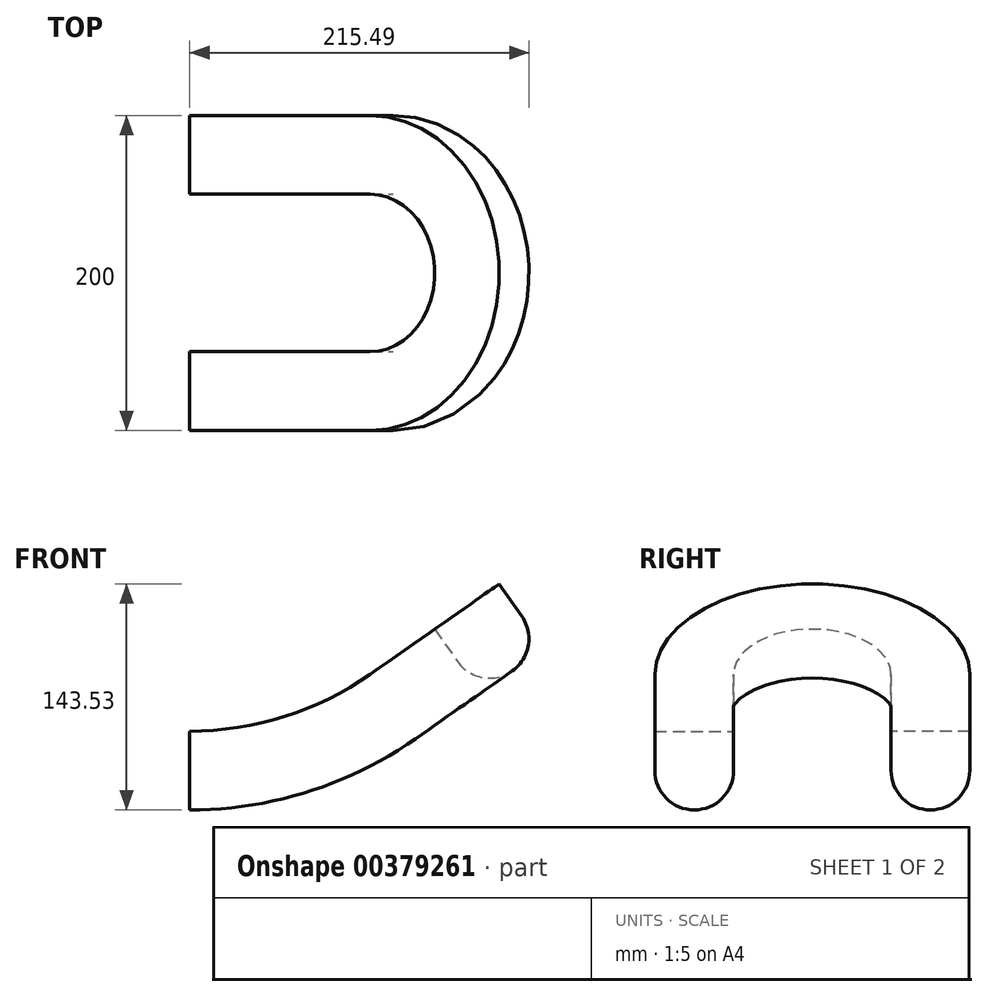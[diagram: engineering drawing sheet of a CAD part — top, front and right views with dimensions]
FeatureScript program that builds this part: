
annotation { "Feature Type Name" : "Feature", "Feature Type Description" : "" }
export const myFeature = defineFeature(function(context is Context, id is Id, definition is map)
    precondition{}
    {
        {
            var Q0;
            Q0=qCreatedBy(makeId("Front.planeOp"),FACE);
            var sketch = newSketch(context, id + "F0", { "sketchPlane" : qUnion([Q0])});
            skArc(sketch, "E0", {"start": v(114.72, -163.83) * mm, "mid": v(60.14, -190.74) * mm, "end": v(0, -200) * mm});
            skLineSegment(sketch, "E1", {"start": v(0, 0) * mm, "end": v(0, -200) * mm});
            skLineSegment(sketch, "E2", {"start": v(0, 0) * mm, "end": v(114.72, -163.83) * mm, "construction": true});
            skLineSegment(sketch, "E3", {"start": v(0, 0) * mm, "end": v(-114.72, -163.83) * mm, "construction": true});
            skArc(sketch, "E4", {"start": v(0, -200) * mm, "mid": v(-60.14, -190.74) * mm, "end": v(-114.72, -163.83) * mm, "construction": true});
            skLineSegment(sketch, "E5", {"start": v(114.72, -163.83) * mm, "end": v(196.63, -106.47) * mm});
            skLineSegment(sketch, "E6", {"start": v(-114.72, -163.83) * mm, "end": v(-196.63, -106.47) * mm, "construction": true});
            skSolve(sketch);
        }
        {
            var Q0;
            Q0=sQuery(id+"F0.wireOp",EDGE,"E5");
            var Q1;
            Q1=sQuery(id+"F0.wireOp",EDGE,"E0");
            extrude(context, id + "F1", {"bodyType" : ToolBodyType.SURFACE, "surfaceEntities" : qUnion([Q0, Q1]), "depth" : 100 * mm});
        }
        {
            var Q0;
            Q0=makeQuery(id+"F1.opExtrude","SWEPT_FACE",FACE,{"disambiguationData":[OSD([sQuery(id+"F0.wireOp",EDGE,"E5")])]});
            var sketch = newSketch(context, id + "F2", { "sketchPlane" : qUnion([Q0])});
            skArc(sketch, "E7", {"start": v(100, 100) * mm, "mid": v(70.71, 29.29) * mm, "end": v(0, 0) * mm});
            skSolve(sketch);
        }
        {
            var Q0;
            Q0=qCreatedBy(makeId("Right.planeOp"),FACE);
            var sketch = newSketch(context, id + "F3", { "sketchPlane" : qUnion([Q0])});
            skLineSegment(sketch, "E8.bottom", {"start": v(0, -200) * mm, "end": v(-50, -200) * mm});
            skLineSegment(sketch, "E8.top", {"start": v(0, -225) * mm, "end": v(-50, -225) * mm, "construction": true});
            skLineSegment(sketch, "E8.left", {"start": v(0, -200) * mm, "end": v(0, -225) * mm});
            skLineSegment(sketch, "E8.right", {"start": v(-50, -200) * mm, "end": v(-50, -225) * mm});
            skArc(sketch, "E9", {"start": v(0, -225) * mm, "mid": v(-25, -250) * mm, "end": v(-50, -225) * mm});
            skSolve(sketch);
        }
        {
            var Q0;
            Q0=makeQuery(id+"F3.imprint","IMPRINT",FACE,{"disambiguationData":[TD([[makeQuery(id+"F3.imprint","IMPRINT",EDGE,{"derivedFrom":sQuery(id+"F3.wireOp",EDGE,"E8.bottom")}),1.0]])]});
            var Q1;
            Q1=makeQuery(id+"F1.opExtrude","CAP_EDGE",EDGE,{"disambiguationData":[OSD([sQuery(id+"F0.wireOp",EDGE,"E0")])],"isStart":true});
            var Q2;
            Q2=sQuery(id+"F2.wireOp",EDGE,"E7");
            sweep(context, id + "F4", {"profiles" : qUnion([Q0]), "path" : qUnion([Q1, Q2])});
        }
        {
            var Q0;
            Q0=makeQuery(id+"F1.opExtrude","CAP_VERTEX",VERTEX,{"disambiguationData":[OSD([sQuery(id+"F0.wireOp",VERTEX,"E5.end")])],"isStart":false});
            var Q1;
            Q1=makeQuery(id+"F1.opExtrude","CAP_VERTEX",VERTEX,{"disambiguationData":[OSD([sQuery(id+"F0.wireOp",VERTEX,"E0.start")])],"isStart":false});
            var Q2;
            Q2=makeQuery(id+"F1.opExtrude","CAP_VERTEX",VERTEX,{"disambiguationData":[OSD([sQuery(id+"F0.wireOp",VERTEX,"E0.end")])],"isStart":false});
            cPlane(context, id + "F5", {"entities" : qUnion([Q0, Q1, Q2]), "cplaneType" : CPlaneType.THREE_POINT, "offset" : 25 * mm, "width" : 150 * mm, "height" : 150 * mm});
        }
        {
            var Q0;
            Q0=makeQuery(id+"F4.opSweep","SWEPT_BODY",BODY,{"disambiguationData":[OSD([sQuery(id+"F2.wireOp",EDGE,"E7"),sQuery(id+"F3.wireOp",EDGE,"E8.bottom"),sQuery(id+"F3.wireOp",EDGE,"E8.left"),sQuery(id+"F3.wireOp",EDGE,"E8.right"),sQuery(id+"F3.wireOp",EDGE,"E9")])]});
            var Q1;
            Q1=qCreatedBy(id+"F5.planeOp",FACE);
            mirror(context, id + "F6", {"operationType" : NewBodyOperationType.ADD, "entities" : qUnion([Q0]), "mirrorPlane" : qUnion([Q1])});
        }
    });
